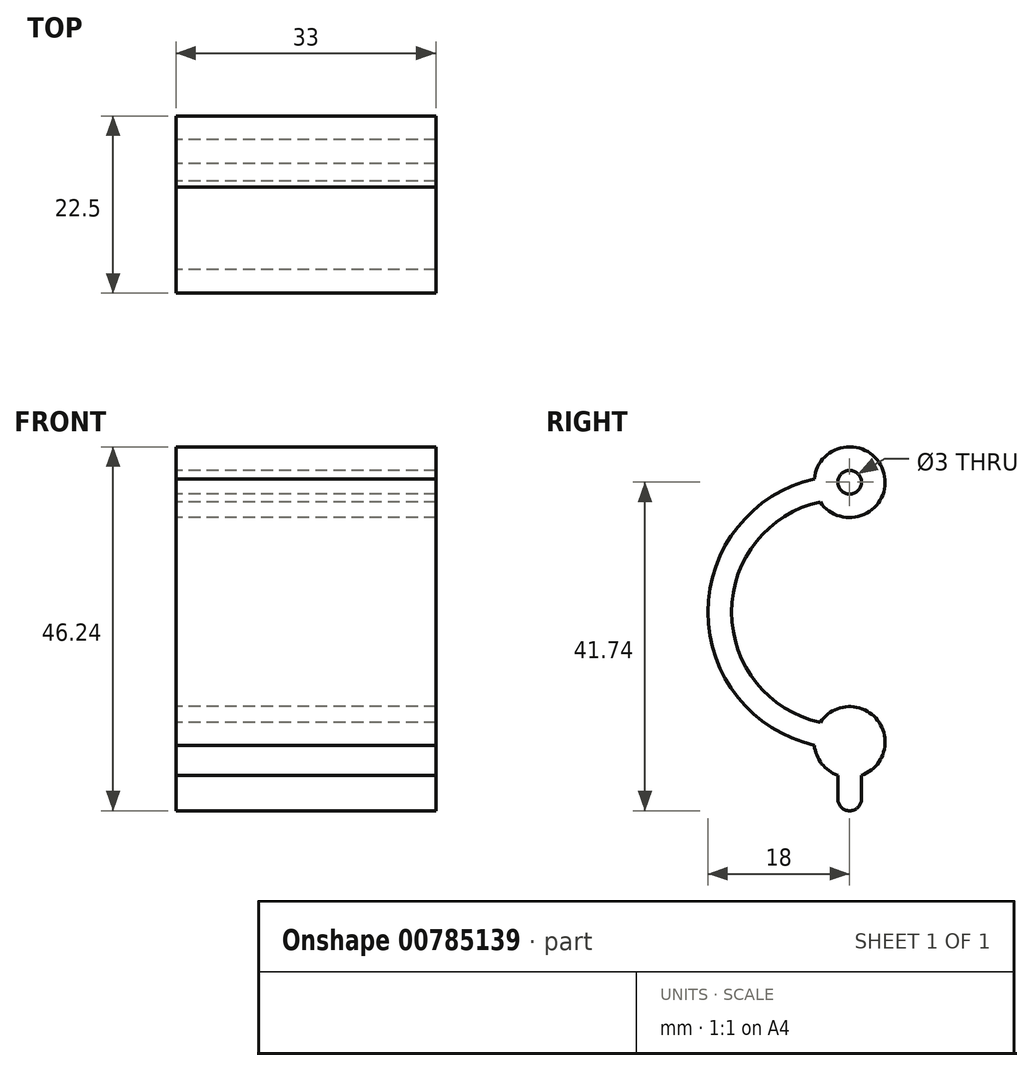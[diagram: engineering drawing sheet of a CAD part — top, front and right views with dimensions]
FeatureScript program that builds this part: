
annotation { "Feature Type Name" : "Feature", "Feature Type Description" : "" }
export const myFeature = defineFeature(function(context is Context, id is Id, definition is map)
    precondition{}
    {
        {
            var Q0;
            Q0=qCreatedBy(makeId("Right.planeOp"),FACE);
            var sketch = newSketch(context, id + "F0", { "sketchPlane" : qUnion([Q0])});
            skLineSegment(sketch, "E0.bottom", {"start": v(0, 0) * mm, "end": v(-15, 0) * mm, "construction": true});
            skLineSegment(sketch, "E0.top", {"start": v(0, 28) * mm, "end": v(-15, 28) * mm, "construction": true});
            skLineSegment(sketch, "E0.left", {"start": v(0, 0) * mm, "end": v(0, 28) * mm, "construction": true});
            skLineSegment(sketch, "E0.right", {"start": v(-15, 0) * mm, "end": v(-15, 28) * mm, "construction": true});
            skArc(sketch, "E1", {"start": v(-3.74, 28) * mm, "mid": v(4.36, 31.6) * mm, "end": v(-4.48, 30.9) * mm});
            skArc(sketch, "E2", {"start": v(-4.48, -2.9) * mm, "mid": v(-3.55, -5.26) * mm, "end": v(-1.5, -6.74) * mm});
            skPoint(sketch, "E3", {"position": v(-15, 14) * mm});
            skArc(sketch, "E4", {"start": v(-3.74, 28) * mm, "mid": v(-15, 14) * mm, "end": v(-3.74, 0) * mm});
            skArc(sketch, "E5", {"start": v(-4.48, 30.9) * mm, "mid": v(-18, 14) * mm, "end": v(-4.48, -2.9) * mm});
            skCircle(sketch, "E6", {"center": v(0, 30.5) * mm, "radius": 1.5 * mm});
            skCircle(sketch, "E7", {"center": v(0, -2.5) * mm, "radius": 1.5 * mm});
            skLineSegment(sketch, "E8.left", {"start": v(-1.5, -6.74) * mm, "end": v(-1.5, -9.74) * mm});
            skLineSegment(sketch, "E8.right", {"start": v(1.5, -6.74) * mm, "end": v(1.5, -9.74) * mm});
            skArc(sketch, "E9", {"start": v(-1.5, -9.74) * mm, "mid": v(0, -11.24) * mm, "end": v(1.5, -9.74) * mm});
            skArc(sketch, "E10.trimOffspring", {"start": v(1.5, -6.74) * mm, "mid": v(3.55, 0.26) * mm, "end": v(-3.74, 0) * mm});
            skSolve(sketch);
        }
        {
            var Q0;
            Q0=makeQuery(id+"F0.imprint","IMPRINT",FACE,{"disambiguationData":[TD([[makeQuery(id+"F0.imprint","IMPRINT",EDGE,{"derivedFrom":sQuery(id+"F0.wireOp",EDGE,"E1")}),1.0]])]});
            var Q1;
            Q1=makeQuery(id+"F0.imprint","IMPRINT",FACE,{"disambiguationData":[TD([[makeQuery(id+"F0.imprint","IMPRINT",EDGE,{"derivedFrom":sQuery(id+"F0.wireOp",EDGE,"E7")}),1.0]])]});
            extrude(context, id + "F1", {"entities" : qUnion([Q0, Q1]), "depth" : 33 * mm, "offsetDistance" : 25 * mm});
        }
    });
